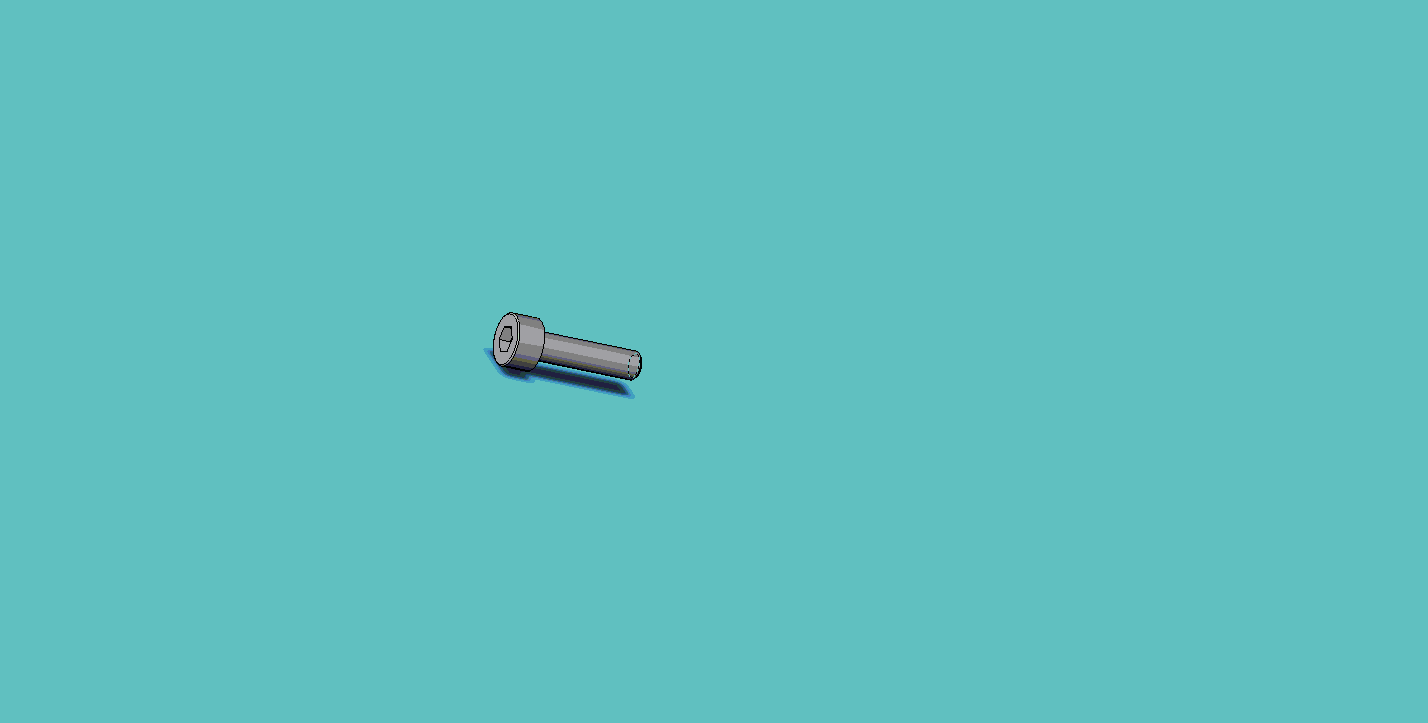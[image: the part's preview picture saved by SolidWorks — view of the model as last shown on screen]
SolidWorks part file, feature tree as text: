
SOLIDWORKS PART (.sldprt)
format: sldprt  version: not decoded by parser v0  size: 197,120 bytes
history: native  units: mm
features: sketch x4, plane x3, fillet x2, cut_revolve x2, material x1, revolve x1, thread x1, cut_extrude x1, pattern_linear x1 (+10 scaffold rows collapsed; 1 parser-record rows omitted)
feature tree (27):
  scaffold x10  (default folders/planes/origin — collapsed)
  material  "Material <not specified>"
  plane  "Plane1"
  plane  "Plane2"
  plane  "Plane3"
  parser-record x1  (decoder bookkeeping rows leaked as tree rows — omitted from the tree; the rows remain in map.json)
  revolve  "Base-Revolve"  [1 undecoded]
  sketch  "BodySke"  dims[c1.Head_fillet_rad=1.016mm c1.Head_top_radius=2.54mm c1.D1=19.05mm c1.Diameter=25.4mm c1.D3=50.8mm c1.D4=22.225mm c2.D4=45.0deg c2.D5=22.225mm c2.Head_ht=3.0mm c2.Length=12.0mm c2.D8=9.525mm c3.D8=45.0deg c3.D1=9.525mm c4.D8=9.525mm c5.D8=45.0deg c5.D1=73.025mm c6.D1=45.0deg c7.D1=9.525mm c8.D1=45.0deg c8.D4=22.225mm c9.D4=45.0deg c9.Thread_min=12.7mm c10.D4=9.525mm c10.Body_ch_ang=45.0deg c10.D8=22.225mm c11.D8=45.0deg c11.D5=22.225mm c12.D5=45.0deg c13.D5=~4.490128mm c14.D5=45.0deg c14.Head_dia=50.8mm c15.D5=~8.980256mm c15.Head_ch_ang=45.0deg c15.Head_side_ht=22.86mm c15.D9=19.05mm c15.Diameter=3.0mm c15.Head_dia=38.1mm c15.Minor_dia=2.439mm c15.Advance=0.5mm c15.Thread_nom=12.0mm c15.Thread_lim=~74.083342mm c15.Thread_length=60.0mm c16.Head_dia=5.5mm]
  thread  "ThreadCosmetic"  Diameter=10.5mm Thread_length=10.5mm Thread_minor=2.439mm  [1 undecoded]
  fillet  "Fillet1"  Radius=0.1mm Head_dia=5.5mm
  fillet  "Fillet2"  Radius=0.15mm
  sketch  "Sketch2"  dims[c1.D1=1.28mm c1.D2=25.4mm c2.D2=60.0deg c2.Wall_thickness=11.427mm c2.Depth=1.3mm]
  cut_revolve  "Hex-PreBroach"  Angle=360deg
  sketch  "Sketch3"  dims[c1.D1=1.28mm c1.D2=1.28mm c1.Hex_size=2.56mm c1.D4=~14.664697mm c2.D4=120.0deg]
  cut_extrude  "Hex"  Depth=1.3mm Key_eng=1.3mm
  sketch  "ThdSchSke"  dims[c1.Thread_minor=~1.03886mm c1.Diameter=~1.413535mm c1.Start=~0.988134mm c1.D4=~4.446753mm c1.Vee=60.0deg c2.Thread_minor=~1.03886mm c2.Start=~2.540025mm c2.D1=~0.108159mm c2.D2=~0.108159mm c3.D1=~0.216319mm c3.SideAngle=55.0deg c3.D2=~0.216319mm c3.VeeAngle=70.0deg c3.Thread_minor=2.439mm c3.Overcut=3.75mm c3.Diameter=3.0mm c3.D6=~8.326268mm c4.D1=~8.326268mm c5.D1=90.0deg c5.Start=54.0mm c6.Start=4.5mm]
  cut_revolve  "ThreadSchematic"  Angle=360deg
  pattern_linear  "ThdSchPat"  Count1=21 Count2=1 Spacing1=0.5mm Spacing2=50mm Num_threads=21 Advance=0.5mm CopiedFlag=1
decode coverage: 11 of 12 modeling features carry decoded parameters
note: ~ marks probable driven/reference dimensions
note: 2 parameter values undecoded
note: suppression state not decoded; provenance and decode notes live in map.json
